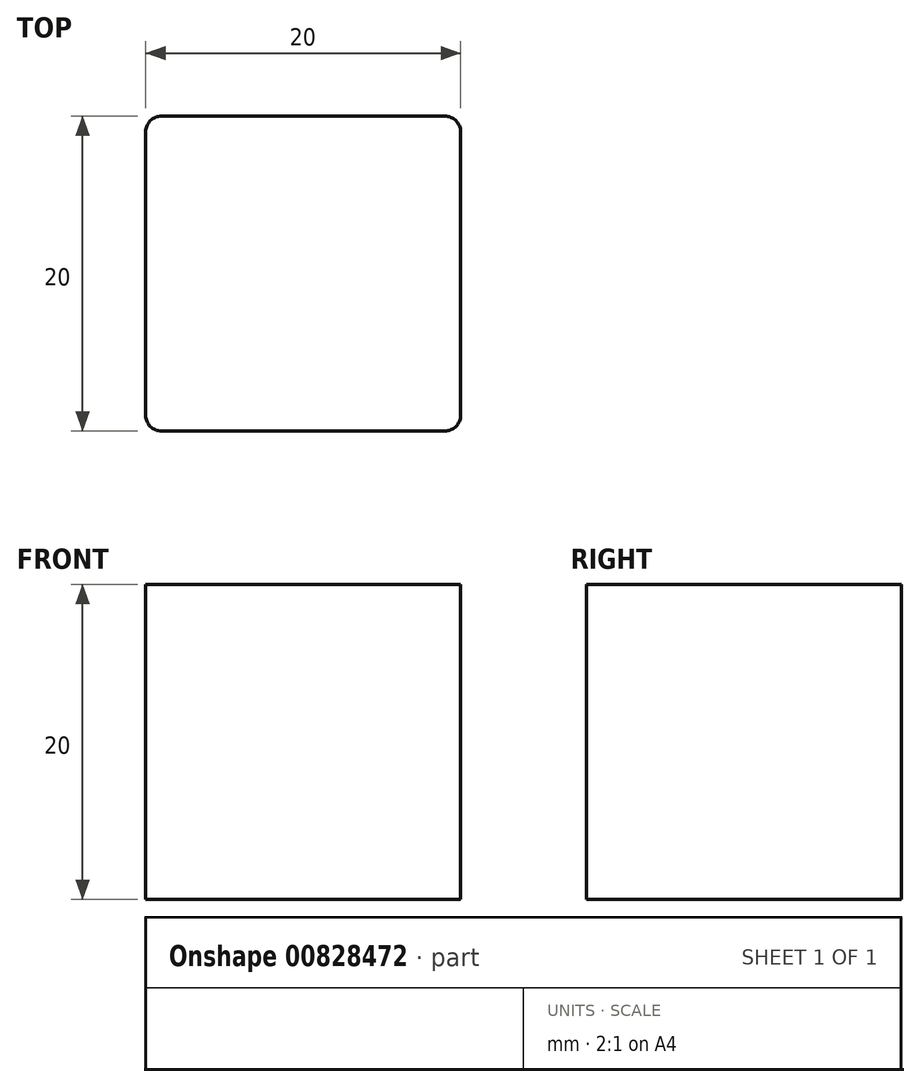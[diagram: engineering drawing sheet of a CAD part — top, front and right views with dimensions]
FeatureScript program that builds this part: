
annotation { "Feature Type Name" : "Feature", "Feature Type Description" : "" }
export const myFeature = defineFeature(function(context is Context, id is Id, definition is map)
    precondition{}
    {
        {
            var Q0;
            Q0=qCreatedBy(makeId("Top.planeOp"),FACE);
            var sketch = newSketch(context, id + "F0", { "sketchPlane" : qUnion([Q0])});
            skLineSegment(sketch, "E0.bottom", {"start": v(1, 0) * mm, "end": v(19, 0) * mm});
            skLineSegment(sketch, "E0.top", {"start": v(1, 20) * mm, "end": v(19, 20) * mm});
            skLineSegment(sketch, "E0.left", {"start": v(0, 1) * mm, "end": v(0, 19) * mm});
            skLineSegment(sketch, "E0.right", {"start": v(20, 1) * mm, "end": v(20, 19) * mm});
            skPoint(sketch, "E1.visualSharp", {"position": v(0, 20) * mm});
            skArc(sketch, "E1.filletArc", {"start": v(1, 20) * mm, "mid": v(0.3, 19.7) * mm, "end": v(0, 19) * mm});
            skPoint(sketch, "E2.visualSharp", {"position": v(20, 20) * mm});
            skArc(sketch, "E2.filletArc", {"start": v(20, 19) * mm, "mid": v(19.7, 19.7) * mm, "end": v(19, 20) * mm});
            skPoint(sketch, "E3.visualSharp", {"position": v(20, 0) * mm});
            skArc(sketch, "E3.filletArc", {"start": v(19, 0) * mm, "mid": v(19.7, 0.3) * mm, "end": v(20, 1) * mm});
            skPoint(sketch, "E4.visualSharp", {"position": v(0, 0) * mm});
            skArc(sketch, "E4.filletArc", {"start": v(0, 1) * mm, "mid": v(0.3, 0.3) * mm, "end": v(1, 0) * mm});
            skSolve(sketch);
        }
        {
            var Q0;
            Q0 = qSketchRegion(id + "F0", true);
            extrude(context, id + "F1", {"entities" : qUnion([Q0]), "depth" : 20 * mm, "offsetDistance" : 25 * mm});
        }
    });
